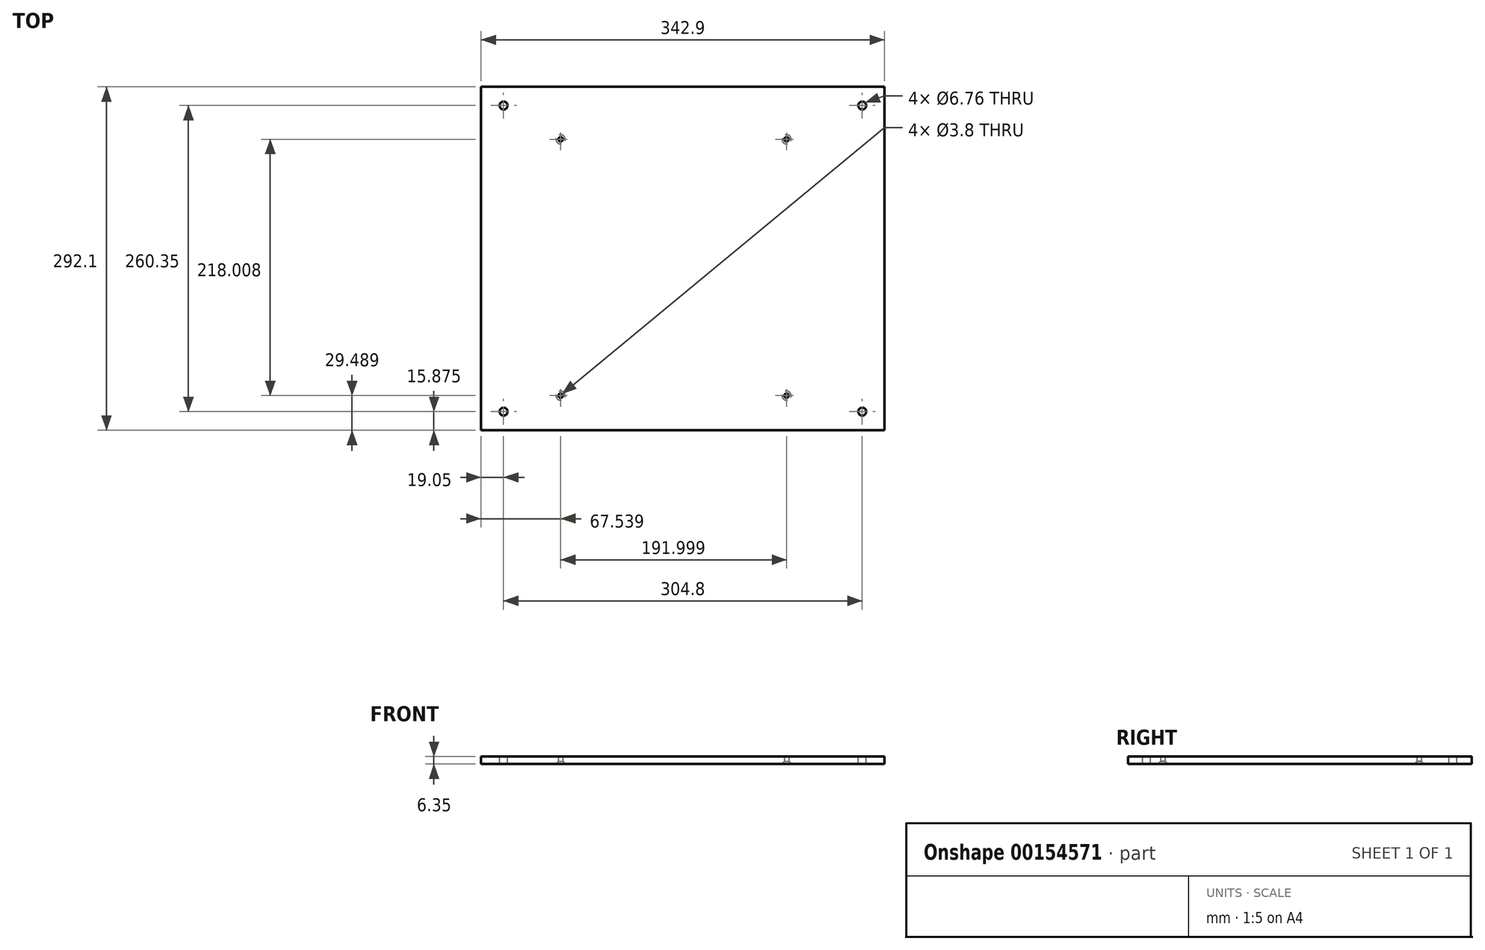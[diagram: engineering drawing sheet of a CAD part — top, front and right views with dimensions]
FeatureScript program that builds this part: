
annotation { "Feature Type Name" : "Feature", "Feature Type Description" : "" }
export const myFeature = defineFeature(function(context is Context, id is Id, definition is map)
    precondition{}
    {
        {
            var Q0;
            Q0=qCreatedBy(makeId("Top.planeOp"),FACE);
            var sketch = newSketch(context, id + "F0", { "sketchPlane" : qUnion([Q0])});
            skLineSegment(sketch, "E0.bottom", {"start": v(-171.45, 146.05) * mm, "end": v(171.45, 146.05) * mm});
            skLineSegment(sketch, "E0.top", {"start": v(-171.45, -146.05) * mm, "end": v(171.45, -146.05) * mm});
            skLineSegment(sketch, "E0.left", {"start": v(-171.45, 146.05) * mm, "end": v(-171.45, -146.05) * mm});
            skLineSegment(sketch, "E0.right", {"start": v(171.45, 146.05) * mm, "end": v(171.45, -146.05) * mm});
            skLineSegment(sketch, "E1", {"start": v(-171.45, 146.05) * mm, "end": v(171.45, -146.05) * mm, "construction": true});
            skSolve(sketch);
        }
        {
            var Q0;
            Q0=makeQuery(id+"F0.imprint","IMPRINT",FACE,{"disambiguationData":[TD([[makeQuery(id+"F0.imprint","IMPRINT",EDGE,{"derivedFrom":sQuery(id+"F0.wireOp",EDGE,"E0.bottom")}),-1.0]])]});
            extrude(context, id + "F1", {"entities" : qUnion([Q0]), "depth" : 6.35 * mm});
        }
        {
            var Q0;
            Q0=makeQuery(id+"F1.opExtrude","CAP_FACE",FACE,{"disambiguationData":[OSD([sQuery(id+"F0.wireOp",EDGE,"E0.bottom"),sQuery(id+"F0.wireOp",EDGE,"E0.top"),sQuery(id+"F0.wireOp",EDGE,"E0.left"),sQuery(id+"F0.wireOp",EDGE,"E0.right")])],"isStart":false});
            var sketch = newSketch(context, id + "F2", { "sketchPlane" : qUnion([Q0])});
            skLineSegment(sketch, "E2", {"start": v(-152.4, 146.05) * mm, "end": v(-152.4, -146.05) * mm, "construction": true});
            skLineSegment(sketch, "E3", {"start": v(152.4, 146.05) * mm, "end": v(152.4, -146.05) * mm, "construction": true});
            skLineSegment(sketch, "E4", {"start": v(171.45, 130.17) * mm, "end": v(-171.45, 130.17) * mm, "construction": true});
            skLineSegment(sketch, "E5", {"start": v(171.45, -130.18) * mm, "end": v(-171.45, -130.18) * mm, "construction": true});
            skCircle(sketch, "E6", {"center": v(-152.4, 130.17) * mm, "radius": 3.38 * mm});
            skCircle(sketch, "E7", {"center": v(152.4, 130.18) * mm, "radius": 3.38 * mm});
            skCircle(sketch, "E8", {"center": v(-152.4, -130.18) * mm, "radius": 3.38 * mm});
            skCircle(sketch, "E9", {"center": v(152.4, -130.18) * mm, "radius": 3.38 * mm});
            skSolve(sketch);
        }
        {
            var Q0;
            Q0=makeQuery(id+"F2.imprint","IMPRINT",FACE,{"disambiguationData":[TD([[makeQuery(id+"F2.imprint","IMPRINT",EDGE,{"derivedFrom":sQuery(id+"F2.wireOp",EDGE,"E6")}),1.0]])]});
            var Q1;
            Q1=makeQuery(id+"F2.imprint","IMPRINT",FACE,{"disambiguationData":[TD([[makeQuery(id+"F2.imprint","IMPRINT",EDGE,{"derivedFrom":sQuery(id+"F2.wireOp",EDGE,"E7")}),1.0]])]});
            var Q2;
            Q2=makeQuery(id+"F2.imprint","IMPRINT",FACE,{"disambiguationData":[TD([[makeQuery(id+"F2.imprint","IMPRINT",EDGE,{"derivedFrom":sQuery(id+"F2.wireOp",EDGE,"E9")}),1.0]])]});
            var Q3;
            Q3=makeQuery(id+"F2.imprint","IMPRINT",FACE,{"disambiguationData":[TD([[makeQuery(id+"F2.imprint","IMPRINT",EDGE,{"derivedFrom":sQuery(id+"F2.wireOp",EDGE,"E8")}),1.0]])]});
            extrude(context, id + "F3", {"entities" : qUnion([Q0, Q1, Q2, Q3]), "operationType" : NewBodyOperationType.REMOVE, "endBound" : BoundingType.THROUGH_ALL, "oppositeDirection" : true, "depth" : 25.4 * mm});
        }
        {
            var Q0;
            Q0=makeQuery(id+"F1.opExtrude","CAP_FACE",FACE,{"disambiguationData":[OSD([sQuery(id+"F0.wireOp",EDGE,"E0.bottom"),sQuery(id+"F0.wireOp",EDGE,"E0.top"),sQuery(id+"F0.wireOp",EDGE,"E0.left"),sQuery(id+"F0.wireOp",EDGE,"E0.right")])],"isStart":true});
            var sketch = newSketch(context, id + "F4", { "sketchPlane" : qUnion([Q0])});
            skLineSegment(sketch, "E10", {"start": v(-171.45, 116.56) * mm, "end": v(171.45, 116.56) * mm, "construction": true});
            skLineSegment(sketch, "E11", {"start": v(-171.45, -101.45) * mm, "end": v(171.45, -101.45) * mm, "construction": true});
            skLineSegment(sketch, "E12", {"start": v(-103.91, 146.05) * mm, "end": v(-103.91, -146.05) * mm, "construction": true});
            skLineSegment(sketch, "E13", {"start": v(88.09, 146.05) * mm, "end": v(88.09, -146.05) * mm, "construction": true});
            skPoint(sketch, "E14", {"position": v(-103.91, 116.56) * mm});
            skPoint(sketch, "E15", {"position": v(88.09, 116.56) * mm});
            skPoint(sketch, "E16", {"position": v(88.09, -101.45) * mm});
            skPoint(sketch, "E17", {"position": v(-103.91, -101.45) * mm});
            skSolve(sketch);
        }
        {
            var Q0;
            Q0=sQuery(id+"F4.wireOp",VERTEX,"E14");
            var Q1;
            Q1=sQuery(id+"F4.wireOp",VERTEX,"E15");
            var Q2;
            Q2=sQuery(id+"F4.wireOp",VERTEX,"E16");
            var Q3;
            Q3=sQuery(id+"F4.wireOp",VERTEX,"E17");
            var Q4;
            Q4=makeQuery(id+"F1.opExtrude","SWEPT_BODY",BODY,{"disambiguationData":[OSD([sQuery(id+"F0.wireOp",EDGE,"E0.bottom"),sQuery(id+"F0.wireOp",EDGE,"E0.top"),sQuery(id+"F0.wireOp",EDGE,"E0.left"),sQuery(id+"F0.wireOp",EDGE,"E0.right")])]});
            hole(context, id + "F5", {"style" : HoleStyle.C_SINK, "endStyle" : HoleEndStyle.THROUGH, "standardTappedOrClearance" : lookupTablePath({ "standard" : "ANSI", "fit" : "Normal (ASME)", "size" : "#6", "type" : "Clearance" }), "standardBlindInLast" : lookupTablePath({ "fit" : "Free", "standard" : "ANSI", "size" : "#6", "type" : "Clearance" }), "holeDiameter" : 3.8 * mm, "cSinkDiameter" : 7.8 * mm, "cSinkAngle" : 82 * degree, "locations" : qUnion([Q0, Q1, Q2, Q3]), "scope" : qUnion([Q4]), "isTappedThrough" : true});
        }
    });
